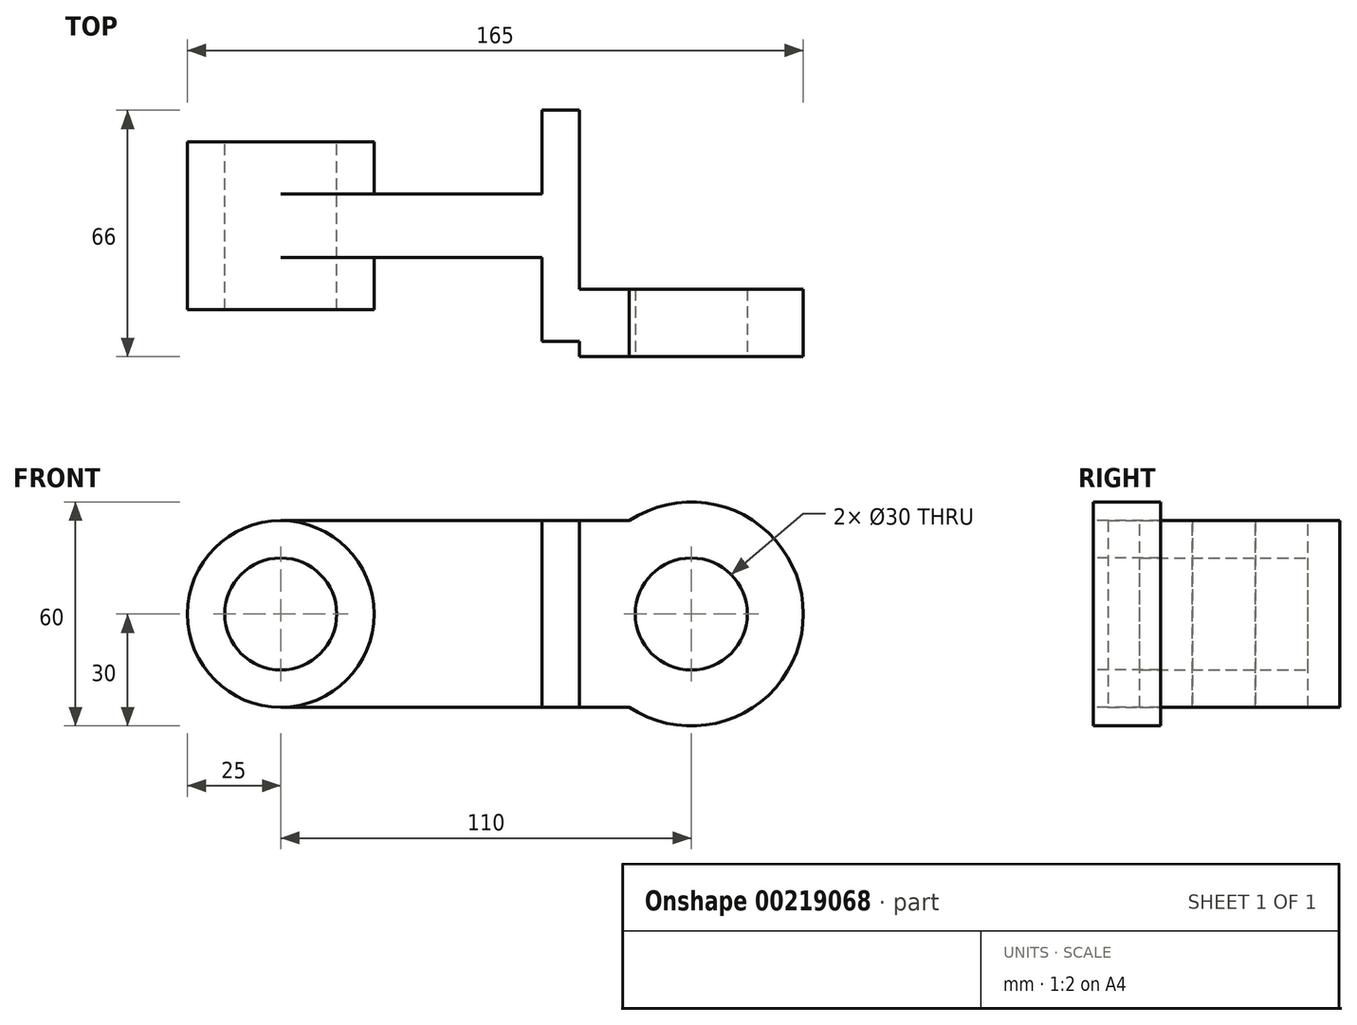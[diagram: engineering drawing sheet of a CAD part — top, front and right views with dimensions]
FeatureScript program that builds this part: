
annotation { "Feature Type Name" : "Feature", "Feature Type Description" : "" }
export const myFeature = defineFeature(function(context is Context, id is Id, definition is map)
    precondition{}
    {
        {
            var Q0;
            Q0=qCreatedBy(makeId("Front.planeOp"),FACE);
            var sketch = newSketch(context, id + "F0", { "sketchPlane" : qUnion([Q0])});
            skCircle(sketch, "E0", {"center": v(0, 0) * mm, "radius": 25 * mm});
            skCircle(sketch, "E1", {"center": v(0, 0) * mm, "radius": 15 * mm});
            skLineSegment(sketch, "E2", {"start": v(0, 25) * mm, "end": v(70, 25) * mm});
            skLineSegment(sketch, "E3", {"start": v(70, 25) * mm, "end": v(70, -25) * mm});
            skLineSegment(sketch, "E4", {"start": v(70, -25) * mm, "end": v(0, -25) * mm});
            skLineSegment(sketch, "E5", {"start": v(70, 25) * mm, "end": v(93.42, 25) * mm});
            skLineSegment(sketch, "E6", {"start": v(93.42, -25) * mm, "end": v(70, -25) * mm});
            skCircle(sketch, "E7", {"center": v(110, 0) * mm, "radius": 15 * mm});
            skPoint(sketch, "E7.centerSnap0", {"position": v(110, 0) * mm});
            skCircle(sketch, "E8", {"center": v(110, 0) * mm, "radius": 30 * mm});
            skPoint(sketch, "E9.start.orphan", {"position": v(110, 25) * mm});
            skPoint(sketch, "E10.orphan", {"position": v(110, -25) * mm});
            skLineSegment(sketch, "E11", {"start": v(80, 25) * mm, "end": v(80, -25) * mm});
            skSolve(sketch);
        }
        {
            var Q0;
            Q0=makeQuery(id+"F0.imprint","IMPRINT",FACE,{"disambiguationData":[TD([[makeQuery(id+"F0.imprint","IMPRINT",EDGE,{"derivedFrom":sQuery(id+"F0.wireOp",EDGE,"E1")}),-1.0]])]});
            extrude(context, id + "F1", {"entities" : qUnion([Q0]), "endBound" : BoundingType.SYMMETRIC, "depth" : 45 * mm});
        }
        {
            var Q0;
            {var subQ0=sQuery(id+"F0.wireOp",EDGE,"E2");Q0=makeQuery(id+"F0.imprint","IMPRINT",FACE,{"disambiguationData":[TD([[makeQuery(id+"F0.imprint","IMPRINT",EDGE,{"derivedFrom":subQ0}),-1.0]])]});}
            extrude(context, id + "F2", {"entities" : qUnion([Q0]), "operationType" : NewBodyOperationType.ADD, "endBound" : BoundingType.SYMMETRIC, "depth" : 17 * mm});
        }
        {
            var Q0;
            {var subQ5=sQuery(id+"F0.wireOp",EDGE,"E3");Q0=makeQuery(id+"F0.imprint","IMPRINT",FACE,{"disambiguationData":[TD([[makeQuery(id+"F0.imprint","IMPRINT",EDGE,{"derivedFrom":subQ5}),1.0]])]});}
            extrude(context, id + "F3", {"entities" : qUnion([Q0]), "operationType" : NewBodyOperationType.ADD, "endBound" : BoundingType.SYMMETRIC, "depth" : (14 + 14 + 34) * mm});
        }
        {
            var Q0;
            Q0=makeQuery(id+"F3.opExtrude","CAP_FACE",FACE,{"disambiguationData":[OSD([sQuery(id+"F0.wireOp",EDGE,"E3"),sQuery(id+"F0.wireOp",EDGE,"E5"),sQuery(id+"F0.wireOp",EDGE,"E6"),sQuery(id+"F0.wireOp",EDGE,"E11")])],"isStart":false});
            cPlane(context, id + "F4", {"entities" : qUnion([Q0]), "cplaneType" : CPlaneType.OFFSET, "offset" : 4 * mm, "width" : 150 * mm, "height" : 150 * mm});
        }
        {
            var Q0;
            Q0=qCreatedBy(id+"F4.planeOp",FACE);
            var sketch = newSketch(context, id + "F5", { "sketchPlane" : qUnion([Q0])});
            skCircle(sketch, "E12.0", {"center": v(110, 0) * mm, "radius": 30 * mm});
            skCircle(sketch, "E13.0", {"center": v(110, 0) * mm, "radius": 15 * mm});
            skLineSegment(sketch, "E14.0", {"start": v(80, 25) * mm, "end": v(93.42, 25) * mm});
            skLineSegment(sketch, "E15.0", {"start": v(93.42, -25) * mm, "end": v(80, -25) * mm});
            skLineSegment(sketch, "E16.0", {"start": v(80, 25) * mm, "end": v(80, -25) * mm});
            skPoint(sketch, "E17.orphan", {"position": v(70, 25) * mm});
            skPoint(sketch, "E18.orphan", {"position": v(70, -25) * mm});
            skSolve(sketch);
        }
        {
            var Q0;
            Q0=makeQuery(id+"F5.imprint","IMPRINT",FACE,{"disambiguationData":[TD([[makeQuery(id+"F5.imprint","IMPRINT",EDGE,{"derivedFrom":sQuery(id+"F5.wireOp",EDGE,"E13.0")}),-1.0]])]});
            var Q1;
            {var subQ0=sQuery(id+"F5.wireOp",EDGE,"E14.0");Q1=makeQuery(id+"F5.imprint","IMPRINT",FACE,{"disambiguationData":[TD([[makeQuery(id+"F5.imprint","IMPRINT",EDGE,{"derivedFrom":subQ0}),-1.0]])]});}
            var Q2;
            {var subQ0=sQuery(id+"F5.wireOp",EDGE,"E15.0");Q2=makeQuery(id+"F5.imprint","IMPRINT",FACE,{"disambiguationData":[TD([[makeQuery(id+"F5.imprint","IMPRINT",EDGE,{"derivedFrom":subQ0}),-1.0]])]});}
            extrude(context, id + "F6", {"entities" : qUnion([Q0, Q1, Q2]), "operationType" : NewBodyOperationType.ADD, "oppositeDirection" : true, "depth" : 18 * mm});
        }
    });
